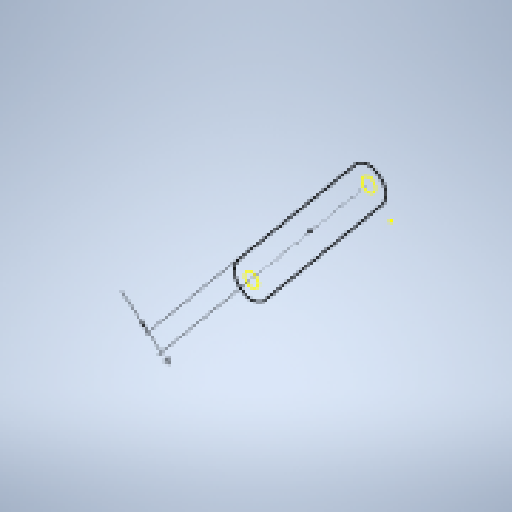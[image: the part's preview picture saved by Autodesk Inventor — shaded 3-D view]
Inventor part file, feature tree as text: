
AUTODESK INVENTOR PART (.ipt)
format: ipt  version: 2024.1 (Build 281209000, 209)  size: 143,872 bytes
history: native  units: mm
features: other x4, reference x2, extrude x1, sketch x1
ambient origin geometry x8: Origin, YZ Plane, XZ Plane, XY Plane, X Axis, Y Axis, Z Axis, Center Point
bodies: Solid1 (feature_tree)
feature tree (8):
  extrude  "Extrusion1"  Depth=2.0mm TaperAngle=0.0deg
  sketch  "Sketch1"  dims[d0=4.0mm d1=2.0mm d2=0.0mm]
  reference  "Reference1"
  reference  "Reference2"
  other  "<userpath>\Documents\0004-CAD\3D-cad-main\the-artifact\artifact-assembly.iam"
  other  "artifact-assembly.iam"
  other  "control-arm:1"
  other  "see-saw-arm:1"
